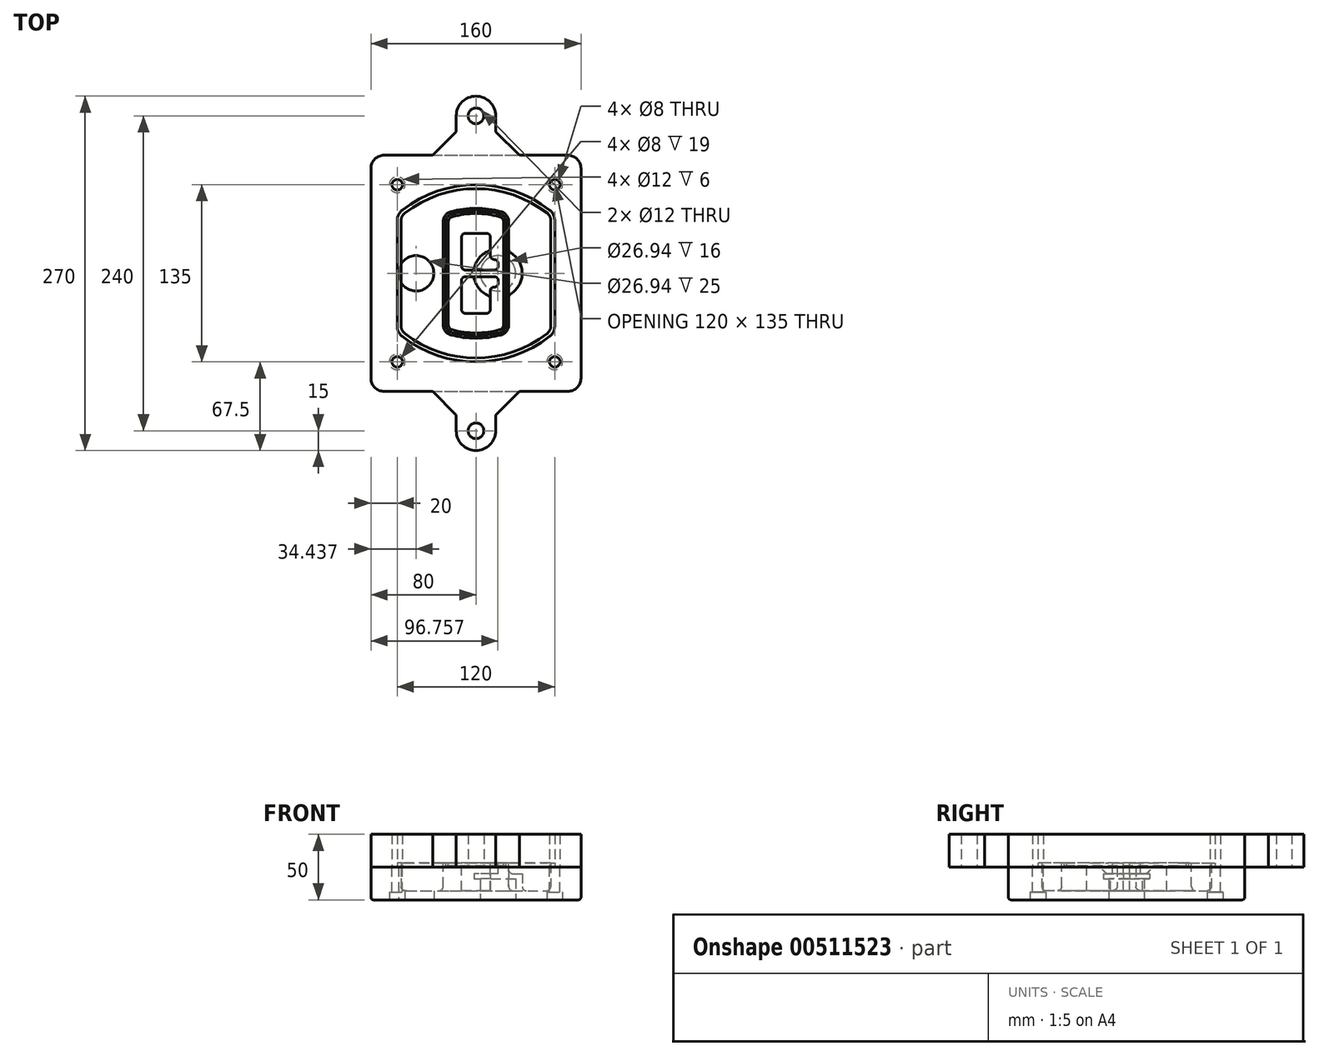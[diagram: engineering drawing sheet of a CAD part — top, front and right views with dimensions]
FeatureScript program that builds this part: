
annotation { "Feature Type Name" : "Feature", "Feature Type Description" : "" }
export const myFeature = defineFeature(function(context is Context, id is Id, definition is map)
    precondition{}
    {
        {
            var Q0;
            Q0=qCreatedBy(makeId("Top.planeOp"),FACE);
            var sketch = newSketch(context, id + "F0", { "sketchPlane" : qUnion([Q0])});
            skPoint(sketch, "E0.rect.middle", {"position": v(0, 0) * mm});
            skLineSegment(sketch, "E1.bottom", {"start": v(-70, -90) * mm, "end": v(70, -90) * mm});
            skLineSegment(sketch, "E1.top", {"start": v(-70, 90) * mm, "end": v(70, 90) * mm});
            skLineSegment(sketch, "E1.left", {"start": v(-80, -80) * mm, "end": v(-80, 80) * mm});
            skLineSegment(sketch, "E1.right", {"start": v(80, -80) * mm, "end": v(80, 80) * mm});
            skLineSegment(sketch, "E2", {"start": v(-80, 90) * mm, "end": v(80, -90) * mm, "construction": true});
            skLineSegment(sketch, "E3", {"start": v(80, 90) * mm, "end": v(-80, -90) * mm, "construction": true});
            skCircle(sketch, "E4", {"center": v(-60, 67.5) * mm, "radius": 4 * mm});
            skCircle(sketch, "E5", {"center": v(60, 67.5) * mm, "radius": 4 * mm});
            skCircle(sketch, "E6", {"center": v(60, -67.5) * mm, "radius": 4 * mm});
            skCircle(sketch, "E7", {"center": v(-60, -67.5) * mm, "radius": 4 * mm});
            skLineSegment(sketch, "E8", {"start": v(-60, 67.5) * mm, "end": v(60, 67.5) * mm, "construction": true});
            skLineSegment(sketch, "E9", {"start": v(60, 67.5) * mm, "end": v(60, -67.5) * mm, "construction": true});
            skLineSegment(sketch, "E10", {"start": v(60, -67.5) * mm, "end": v(-60, -67.5) * mm, "construction": true});
            skLineSegment(sketch, "E11", {"start": v(-60, -67.5) * mm, "end": v(-60, 67.5) * mm, "construction": true});
            skLineSegment(sketch, "E12", {"start": v(-60, 40.3) * mm, "end": v(-60, -40.3) * mm});
            skLineSegment(sketch, "E13", {"start": v(60, 40.3) * mm, "end": v(60, -40.3) * mm});
            skArc(sketch, "E14", {"start": v(56.15, 48.18) * mm, "mid": v(0, 67.5) * mm, "end": v(-56.15, 48.18) * mm});
            skArc(sketch, "E15", {"start": v(-56.15, -48.18) * mm, "mid": v(0, -67.5) * mm, "end": v(56.15, -48.18) * mm});
            skLineSegment(sketch, "E16", {"start": v(-60, 0) * mm, "end": v(60, 0) * mm, "construction": true});
            skPoint(sketch, "E17.visualSharp", {"position": v(-60, -45) * mm});
            skArc(sketch, "E17.filletArc", {"start": v(-60, -40.3) * mm, "mid": v(-58.99, -44.68) * mm, "end": v(-56.15, -48.18) * mm});
            skPoint(sketch, "E18.visualSharp", {"position": v(-60, 45) * mm});
            skArc(sketch, "E18.filletArc", {"start": v(-56.15, 48.18) * mm, "mid": v(-58.99, 44.68) * mm, "end": v(-60, 40.3) * mm});
            skPoint(sketch, "E19.visualSharp", {"position": v(60, 45) * mm});
            skArc(sketch, "E19.filletArc", {"start": v(60, 40.3) * mm, "mid": v(58.99, 44.68) * mm, "end": v(56.15, 48.18) * mm});
            skPoint(sketch, "E20.visualSharp", {"position": v(60, -45) * mm});
            skArc(sketch, "E20.filletArc", {"start": v(56.15, -48.18) * mm, "mid": v(58.99, -44.68) * mm, "end": v(60, -40.3) * mm});
            skPoint(sketch, "E21.visualSharp", {"position": v(-80, 90) * mm});
            skArc(sketch, "E21.filletArc", {"start": v(-70, 90) * mm, "mid": v(-77.07, 87.07) * mm, "end": v(-80, 80) * mm});
            skPoint(sketch, "E22.visualSharp", {"position": v(80, 90) * mm});
            skArc(sketch, "E22.filletArc", {"start": v(80, 80) * mm, "mid": v(77.07, 87.07) * mm, "end": v(70, 90) * mm});
            skPoint(sketch, "E23.visualSharp", {"position": v(80, -90) * mm});
            skArc(sketch, "E23.filletArc", {"start": v(70, -90) * mm, "mid": v(77.07, -87.07) * mm, "end": v(80, -80) * mm});
            skPoint(sketch, "E24.visualSharp", {"position": v(-80, -90) * mm});
            skArc(sketch, "E24.filletArc", {"start": v(-80, -80) * mm, "mid": v(-77.07, -87.07) * mm, "end": v(-70, -90) * mm});
            skArc(sketch, "E25.0", {"start": v(57, 40.3) * mm, "mid": v(56.3, 43.36) * mm, "end": v(54.3, 45.81) * mm});
            skLineSegment(sketch, "E25.1", {"start": v(57, 40.3) * mm, "end": v(57, -40.3) * mm});
            skArc(sketch, "E25.2", {"start": v(54.3, -45.81) * mm, "mid": v(56.3, -43.36) * mm, "end": v(57, -40.3) * mm});
            skArc(sketch, "E25.3", {"start": v(-54.3, -45.81) * mm, "mid": v(0, -64.5) * mm, "end": v(54.3, -45.81) * mm});
            skArc(sketch, "E25.4", {"start": v(-57, -40.3) * mm, "mid": v(-56.3, -43.36) * mm, "end": v(-54.3, -45.81) * mm});
            skArc(sketch, "E25.5", {"start": v(54.3, 45.81) * mm, "mid": v(0, 64.5) * mm, "end": v(-54.3, 45.81) * mm});
            skLineSegment(sketch, "E25.6", {"start": v(-57, 40.3) * mm, "end": v(-57, -40.3) * mm});
            skArc(sketch, "E25.7", {"start": v(-54.3, 45.81) * mm, "mid": v(-56.3, 43.36) * mm, "end": v(-57, 40.3) * mm});
            skArc(sketch, "E26.0", {"start": v(-58.62, 51.33) * mm, "mid": v(-62.58, 46.43) * mm, "end": v(-64, 40.3) * mm});
            skArc(sketch, "E26.1", {"start": v(58.62, 51.33) * mm, "mid": v(0, 71.5) * mm, "end": v(-58.62, 51.33) * mm});
            skArc(sketch, "E26.2", {"start": v(64, 40.3) * mm, "mid": v(62.58, 46.43) * mm, "end": v(58.62, 51.33) * mm});
            skLineSegment(sketch, "E26.3", {"start": v(64, 40.3) * mm, "end": v(64, -40.3) * mm});
            skArc(sketch, "E26.4", {"start": v(58.62, -51.33) * mm, "mid": v(62.58, -46.43) * mm, "end": v(64, -40.3) * mm});
            skLineSegment(sketch, "E26.5", {"start": v(-64, 40.3) * mm, "end": v(-64, -40.3) * mm});
            skArc(sketch, "E26.6", {"start": v(-58.62, -51.33) * mm, "mid": v(0, -71.5) * mm, "end": v(58.62, -51.33) * mm});
            skArc(sketch, "E26.7", {"start": v(-64, -40.3) * mm, "mid": v(-62.58, -46.43) * mm, "end": v(-58.62, -51.33) * mm});
            skSolve(sketch);
        }
        {
            var Q0;
            Q0=makeQuery(id+"F0.imprint","IMPRINT",FACE,{"disambiguationData":[TD([[makeQuery(id+"F0.imprint","IMPRINT",EDGE,{"derivedFrom":sQuery(id+"F0.wireOp",EDGE,"E1.bottom")}),1.0]])]});
            var Q1;
            Q1=makeQuery(id+"F0.imprint","IMPRINT",FACE,{"disambiguationData":[TD([[makeQuery(id+"F0.imprint","IMPRINT",EDGE,{"derivedFrom":sQuery(id+"F0.wireOp",EDGE,"E12")}),1.0]])]});
            var Q2;
            Q2=makeQuery(id+"F0.imprint","IMPRINT",FACE,{"disambiguationData":[TD([[makeQuery(id+"F0.imprint","IMPRINT",EDGE,{"derivedFrom":sQuery(id+"F0.wireOp",EDGE,"E25.0")}),1.0]])]});
            var Q3;
            Q3=makeQuery(id+"F0.imprint","IMPRINT",FACE,{"disambiguationData":[TD([[makeQuery(id+"F0.imprint","IMPRINT",EDGE,{"derivedFrom":sQuery(id+"F0.wireOp",EDGE,"E12")}),-1.0]])]});
            extrude(context, id + "F1", {"entities" : qUnion([Q0, Q1, Q2, Q3]), "oppositeDirection" : true, "depth" : 25 * mm});
        }
        {
            var Q0;
            Q0=makeQuery(id+"F0.imprint","IMPRINT",FACE,{"disambiguationData":[TD([[makeQuery(id+"F0.imprint","IMPRINT",EDGE,{"derivedFrom":sQuery(id+"F0.wireOp",EDGE,"E12")}),1.0]])]});
            extrude(context, id + "F2", {"entities" : qUnion([Q0]), "operationType" : NewBodyOperationType.ADD, "depth" : 3 * mm});
        }
        {
            var Q0;
            Q0=makeQuery(id+"F0.imprint","IMPRINT",FACE,{"disambiguationData":[TD([[makeQuery(id+"F0.imprint","IMPRINT",EDGE,{"derivedFrom":sQuery(id+"F0.wireOp",EDGE,"E25.0")}),1.0]])]});
            extrude(context, id + "F3", {"entities" : qUnion([Q0]), "operationType" : NewBodyOperationType.REMOVE, "oppositeDirection" : true, "depth" : 18 * mm});
        }
        {
            var Q0;
            Q0=makeQuery(id+"F2.opExtrude","CAP_FACE",FACE,{"disambiguationData":[OSD([sQuery(id+"F0.wireOp",EDGE,"E12"),sQuery(id+"F0.wireOp",EDGE,"E13"),sQuery(id+"F0.wireOp",EDGE,"E14"),sQuery(id+"F0.wireOp",EDGE,"E15"),sQuery(id+"F0.wireOp",EDGE,"E17.filletArc"),sQuery(id+"F0.wireOp",EDGE,"E18.filletArc"),sQuery(id+"F0.wireOp",EDGE,"E19.filletArc"),sQuery(id+"F0.wireOp",EDGE,"E20.filletArc"),sQuery(id+"F0.wireOp",EDGE,"E25.0"),sQuery(id+"F0.wireOp",EDGE,"E25.1"),sQuery(id+"F0.wireOp",EDGE,"E25.2"),sQuery(id+"F0.wireOp",EDGE,"E25.3"),sQuery(id+"F0.wireOp",EDGE,"E25.4"),sQuery(id+"F0.wireOp",EDGE,"E25.5"),sQuery(id+"F0.wireOp",EDGE,"E25.6"),sQuery(id+"F0.wireOp",EDGE,"E25.7")])],"isStart":false});
            var sketch = newSketch(context, id + "F4", { "sketchPlane" : qUnion([Q0])});
            skArc(sketch, "E27.0", {"start": v(-19.08, -46.97) * mm, "mid": v(0, -49.5) * mm, "end": v(19.08, -46.97) * mm});
            skArc(sketch, "E28.0", {"start": v(19.08, 46.97) * mm, "mid": v(0, 49.5) * mm, "end": v(-19.08, 46.97) * mm});
            skLineSegment(sketch, "E29", {"start": v(-25, 39.25) * mm, "end": v(-25, -39.25) * mm});
            skLineSegment(sketch, "E30", {"start": v(25, 39.25) * mm, "end": v(25, -39.25) * mm});
            skLineSegment(sketch, "E31", {"start": v(-25, 45.1) * mm, "end": v(25, 45.1) * mm, "construction": true});
            skLineSegment(sketch, "E32", {"start": v(-25, -45.1) * mm, "end": v(25, -45.1) * mm, "construction": true});
            skPoint(sketch, "E33.visualSharp", {"position": v(-25, 45.1) * mm});
            skArc(sketch, "E33.filletArc", {"start": v(-19.08, 46.97) * mm, "mid": v(-23.35, 44.11) * mm, "end": v(-25, 39.25) * mm});
            skPoint(sketch, "E34.visualSharp", {"position": v(25, 45.1) * mm});
            skArc(sketch, "E34.filletArc", {"start": v(25, 39.25) * mm, "mid": v(23.35, 44.11) * mm, "end": v(19.08, 46.97) * mm});
            skPoint(sketch, "E35.visualSharp", {"position": v(25, -45.1) * mm});
            skArc(sketch, "E35.filletArc", {"start": v(19.08, -46.97) * mm, "mid": v(23.35, -44.11) * mm, "end": v(25, -39.25) * mm});
            skPoint(sketch, "E36.visualSharp", {"position": v(-25, -45.1) * mm});
            skArc(sketch, "E36.filletArc", {"start": v(-25, -39.25) * mm, "mid": v(-23.35, -44.11) * mm, "end": v(-19.08, -46.97) * mm});
            skArc(sketch, "E37.0", {"start": v(54.3, 45.81) * mm, "mid": v(0, 64.5) * mm, "end": v(-54.3, 45.81) * mm});
            skArc(sketch, "E37.1", {"start": v(-54.3, 45.81) * mm, "mid": v(-56.3, 43.36) * mm, "end": v(-57, 40.3) * mm});
            skLineSegment(sketch, "E37.2", {"start": v(-57, 40.3) * mm, "end": v(-57, -40.3) * mm});
            skArc(sketch, "E37.3", {"start": v(-57, -40.3) * mm, "mid": v(-56.3, -43.36) * mm, "end": v(-54.3, -45.81) * mm});
            skArc(sketch, "E37.4", {"start": v(-54.3, -45.81) * mm, "mid": v(0, -64.5) * mm, "end": v(54.3, -45.81) * mm});
            skArc(sketch, "E37.5", {"start": v(54.3, -45.81) * mm, "mid": v(56.3, -43.36) * mm, "end": v(57, -40.3) * mm});
            skLineSegment(sketch, "E37.6", {"start": v(57, 40.3) * mm, "end": v(57, -40.3) * mm});
            skArc(sketch, "E37.7", {"start": v(57, 40.3) * mm, "mid": v(56.3, 43.36) * mm, "end": v(54.3, 45.81) * mm});
            skLineSegment(sketch, "E38.0", {"start": v(23, 39.25) * mm, "end": v(23, -39.25) * mm});
            skArc(sketch, "E38.1", {"start": v(18.56, -45.04) * mm, "mid": v(21.76, -42.9) * mm, "end": v(23, -39.25) * mm});
            skArc(sketch, "E38.2", {"start": v(-18.56, -45.04) * mm, "mid": v(0, -47.5) * mm, "end": v(18.56, -45.04) * mm});
            skArc(sketch, "E38.3", {"start": v(-23, -39.25) * mm, "mid": v(-21.76, -42.9) * mm, "end": v(-18.56, -45.04) * mm});
            skLineSegment(sketch, "E38.4", {"start": v(-23, 39.25) * mm, "end": v(-23, -39.25) * mm});
            skArc(sketch, "E38.5", {"start": v(23, 39.25) * mm, "mid": v(21.76, 42.9) * mm, "end": v(18.56, 45.04) * mm});
            skArc(sketch, "E38.6", {"start": v(-18.56, 45.04) * mm, "mid": v(-21.76, 42.9) * mm, "end": v(-23, 39.25) * mm});
            skArc(sketch, "E38.7", {"start": v(18.56, 45.04) * mm, "mid": v(0, 47.5) * mm, "end": v(-18.56, 45.04) * mm});
            skArc(sketch, "E39.0", {"start": v(21, 39.25) * mm, "mid": v(20.18, 41.68) * mm, "end": v(18.04, 43.1) * mm});
            skLineSegment(sketch, "E39.1", {"start": v(21, 39.25) * mm, "end": v(21, -39.25) * mm});
            skArc(sketch, "E39.2", {"start": v(18.04, -43.1) * mm, "mid": v(20.18, -41.68) * mm, "end": v(21, -39.25) * mm});
            skArc(sketch, "E39.3", {"start": v(-18.04, -43.1) * mm, "mid": v(0, -45.5) * mm, "end": v(18.04, -43.1) * mm});
            skArc(sketch, "E39.4", {"start": v(-21, -39.25) * mm, "mid": v(-20.18, -41.68) * mm, "end": v(-18.04, -43.1) * mm});
            skArc(sketch, "E39.5", {"start": v(18.04, 43.1) * mm, "mid": v(0, 45.5) * mm, "end": v(-18.04, 43.1) * mm});
            skLineSegment(sketch, "E39.6", {"start": v(-21, 39.25) * mm, "end": v(-21, -39.25) * mm});
            skArc(sketch, "E39.7", {"start": v(-18.04, 43.1) * mm, "mid": v(-20.18, 41.68) * mm, "end": v(-21, 39.25) * mm});
            skLineSegment(sketch, "E40", {"start": v(-25, 0) * mm, "end": v(25, 0) * mm, "construction": true});
            skLineSegment(sketch, "E41", {"start": v(-11, 5.5) * mm, "end": v(-11, 27.5) * mm});
            skLineSegment(sketch, "E42", {"start": v(-8, 30.5) * mm, "end": v(8, 30.5) * mm});
            skLineSegment(sketch, "E43", {"start": v(11, 27.5) * mm, "end": v(11, 13.5) * mm});
            skLineSegment(sketch, "E44", {"start": v(14, 10.5) * mm, "end": v(14, 10.5) * mm});
            skLineSegment(sketch, "E45", {"start": v(17, 7.5) * mm, "end": v(17, 5.5) * mm});
            skLineSegment(sketch, "E46", {"start": v(14, 2.5) * mm, "end": v(-8, 2.5) * mm});
            skPoint(sketch, "E47.visualSharp", {"position": v(-11, 30.5) * mm});
            skArc(sketch, "E47.filletArc", {"start": v(-8, 30.5) * mm, "mid": v(-10.12, 29.62) * mm, "end": v(-11, 27.5) * mm});
            skPoint(sketch, "E48.visualSharp", {"position": v(11, 30.5) * mm});
            skArc(sketch, "E48.filletArc", {"start": v(11, 27.5) * mm, "mid": v(10.12, 29.62) * mm, "end": v(8, 30.5) * mm});
            skPoint(sketch, "E49.visualSharp", {"position": v(11, 10.5) * mm});
            skArc(sketch, "E49.filletArc", {"start": v(11, 13.5) * mm, "mid": v(11.88, 11.38) * mm, "end": v(14, 10.5) * mm});
            skPoint(sketch, "E50.visualSharp", {"position": v(17, 10.5) * mm});
            skArc(sketch, "E50.filletArc", {"start": v(17, 7.5) * mm, "mid": v(16.12, 9.62) * mm, "end": v(14, 10.5) * mm});
            skPoint(sketch, "E51.visualSharp", {"position": v(17, 2.5) * mm});
            skArc(sketch, "E51.filletArc", {"start": v(14, 2.5) * mm, "mid": v(16.12, 3.38) * mm, "end": v(17, 5.5) * mm});
            skPoint(sketch, "E52.visualSharp", {"position": v(-11, 2.5) * mm});
            skArc(sketch, "E52.filletArc", {"start": v(-11, 5.5) * mm, "mid": v(-10.12, 3.38) * mm, "end": v(-8, 2.5) * mm});
            skLineSegment(sketch, "E53.0.MirrorCS", {"start": v(14, -2.5) * mm, "end": v(-8, -2.5) * mm});
            skArc(sketch, "E54.0.MirrorCS", {"start": v(-11, -5.5) * mm, "mid": v(-10.12, -3.38) * mm, "end": v(-8, -2.5) * mm});
            skLineSegment(sketch, "E55.0.MirrorCS", {"start": v(-11, -5.5) * mm, "end": v(-11, -27.5) * mm});
            skArc(sketch, "E56.0.MirrorCS", {"start": v(-8, -30.5) * mm, "mid": v(-10.12, -29.62) * mm, "end": v(-11, -27.5) * mm});
            skLineSegment(sketch, "E57.0.MirrorCS", {"start": v(-8, -30.5) * mm, "end": v(8, -30.5) * mm});
            skArc(sketch, "E58.0.MirrorCS", {"start": v(11, -27.5) * mm, "mid": v(10.12, -29.62) * mm, "end": v(8, -30.5) * mm});
            skLineSegment(sketch, "E59.0.MirrorCS", {"start": v(11, -27.5) * mm, "end": v(11, -13.5) * mm});
            skArc(sketch, "E60.0.MirrorCS", {"start": v(11, -13.5) * mm, "mid": v(11.88, -11.38) * mm, "end": v(14, -10.5) * mm});
            skArc(sketch, "E61.0.MirrorCS", {"start": v(17, -7.5) * mm, "mid": v(16.12, -9.62) * mm, "end": v(14, -10.5) * mm});
            skLineSegment(sketch, "E62.0.MirrorCS", {"start": v(17, -7.5) * mm, "end": v(17, -5.5) * mm});
            skArc(sketch, "E63.0.MirrorCS", {"start": v(14, -2.5) * mm, "mid": v(16.12, -3.38) * mm, "end": v(17, -5.5) * mm});
            skSolve(sketch);
        }
        {
            var Q0;
            Q0=makeQuery(id+"F4.imprint","IMPRINT",FACE,{"disambiguationData":[TD([[makeQuery(id+"F4.imprint","IMPRINT",EDGE,{"derivedFrom":sQuery(id+"F4.wireOp",EDGE,"E27.0")}),1.0]])]});
            var Q1;
            Q1=makeQuery(id+"F4.imprint","IMPRINT",FACE,{"disambiguationData":[TD([[makeQuery(id+"F4.imprint","IMPRINT",EDGE,{"derivedFrom":sQuery(id+"F4.wireOp",EDGE,"E38.0")}),-1.0]])]});
            var Q2;
            Q2=makeQuery(id+"F4.imprint","IMPRINT",FACE,{"disambiguationData":[TD([[makeQuery(id+"F4.imprint","IMPRINT",EDGE,{"derivedFrom":sQuery(id+"F4.wireOp",EDGE,"E39.0")}),1.0]])]});
            extrude(context, id + "F5", {"entities" : qUnion([Q0, Q1, Q2]), "operationType" : NewBodyOperationType.ADD, "endBound" : BoundingType.UP_TO_NEXT, "oppositeDirection" : true, "depth" : 25 * mm});
        }
        {
            var Q0;
            Q0=makeQuery(id+"F4.imprint","IMPRINT",FACE,{"disambiguationData":[TD([[makeQuery(id+"F4.imprint","IMPRINT",EDGE,{"derivedFrom":sQuery(id+"F4.wireOp",EDGE,"E38.0")}),-1.0]])]});
            extrude(context, id + "F6", {"entities" : qUnion([Q0]), "operationType" : NewBodyOperationType.REMOVE, "oppositeDirection" : true, "depth" : 2 * mm});
        }
        {
            var Q0;
            Q0=makeQuery(id+"F1.opExtrude","CAP_FACE",FACE,{"disambiguationData":[OSD([sQuery(id+"F0.wireOp",EDGE,"E1.bottom"),sQuery(id+"F0.wireOp",EDGE,"E1.top"),sQuery(id+"F0.wireOp",EDGE,"E1.left"),sQuery(id+"F0.wireOp",EDGE,"E1.right"),sQuery(id+"F0.wireOp",EDGE,"E4"),sQuery(id+"F0.wireOp",EDGE,"E5"),sQuery(id+"F0.wireOp",EDGE,"E6"),sQuery(id+"F0.wireOp",EDGE,"E7"),sQuery(id+"F0.wireOp",EDGE,"E21.filletArc"),sQuery(id+"F0.wireOp",EDGE,"E22.filletArc"),sQuery(id+"F0.wireOp",EDGE,"E23.filletArc"),sQuery(id+"F0.wireOp",EDGE,"E24.filletArc")])],"isStart":false});
            var sketch = newSketch(context, id + "F7", { "sketchPlane" : qUnion([Q0])});
            skCircle(sketch, "E64", {"center": v(16.76, 0) * mm, "radius": 13.47 * mm});
            skCircle(sketch, "E65", {"center": v(-45.56, 0) * mm, "radius": 13.47 * mm});
            skLineSegment(sketch, "E66", {"start": v(80, 0) * mm, "end": v(-80, 0) * mm});
            skCircle(sketch, "E67", {"center": v(16.76, 0) * mm, "radius": 18.47 * mm});
            skCircle(sketch, "E68", {"center": v(60, -67.5) * mm, "radius": 6 * mm});
            skCircle(sketch, "E69", {"center": v(-60, -67.5) * mm, "radius": 6 * mm});
            skCircle(sketch, "E70", {"center": v(-60, 67.5) * mm, "radius": 6 * mm});
            skCircle(sketch, "E71", {"center": v(60, 67.5) * mm, "radius": 6 * mm});
            skSolve(sketch);
        }
        {
            var Q0;
            {var subQ1=sQuery(id+"F7.wireOp",EDGE,"E66");var subQ4=sQuery(id+"F7.wireOp",EDGE,"E64");var subQ6=makeQuery(id+"F7.imprint","INTERSECT",VERTEX,{"disambiguationData":[OD(0.0)],"derivedFrom":[subQ4,subQ1]});Q0=makeQuery(id+"F7.imprint","IMPRINT",FACE,{"disambiguationData":[TD([[makeQuery(id+"F7.imprint","IMPRINT",EDGE,{"disambiguationData":[TD([[subQ6,-1.0]])],"derivedFrom":subQ4}),-1.0]])]});}
            var Q1;
            {var subQ0=sQuery(id+"F7.wireOp",EDGE,"E66");var subQ1=sQuery(id+"F7.wireOp",EDGE,"E64");var subQ3=makeQuery(id+"F7.imprint","INTERSECT",VERTEX,{"disambiguationData":[OD(0.0)],"derivedFrom":[subQ1,subQ0]});Q1=makeQuery(id+"F7.imprint","IMPRINT",FACE,{"disambiguationData":[TD([[makeQuery(id+"F7.imprint","IMPRINT",EDGE,{"disambiguationData":[TD([[subQ3,-1.0]])],"derivedFrom":subQ1}),1.0]])]});}
            var Q2;
            {var subQ0=sQuery(id+"F7.wireOp",EDGE,"E66");var subQ1=sQuery(id+"F7.wireOp",EDGE,"E64");var subQ3=makeQuery(id+"F7.imprint","INTERSECT",VERTEX,{"disambiguationData":[OD(0.0)],"derivedFrom":[subQ1,subQ0]});Q2=makeQuery(id+"F7.imprint","IMPRINT",FACE,{"disambiguationData":[TD([[makeQuery(id+"F7.imprint","IMPRINT",EDGE,{"disambiguationData":[TD([[subQ3,1.0]])],"derivedFrom":subQ1}),1.0]])]});}
            var Q3;
            {var subQ1=sQuery(id+"F7.wireOp",EDGE,"E66");var subQ4=sQuery(id+"F7.wireOp",EDGE,"E64");var subQ6=makeQuery(id+"F7.imprint","INTERSECT",VERTEX,{"disambiguationData":[OD(0.0)],"derivedFrom":[subQ4,subQ1]});Q3=makeQuery(id+"F7.imprint","IMPRINT",FACE,{"disambiguationData":[TD([[makeQuery(id+"F7.imprint","IMPRINT",EDGE,{"disambiguationData":[TD([[subQ6,1.0]])],"derivedFrom":subQ4}),-1.0]])]});}
            extrude(context, id + "F8", {"entities" : qUnion([Q0, Q1, Q2, Q3]), "operationType" : NewBodyOperationType.ADD, "oppositeDirection" : true, "depth" : 20 * mm});
        }
        {
            var Q0;
            {var subQ0=sQuery(id+"F7.wireOp",EDGE,"E66");var subQ1=sQuery(id+"F7.wireOp",EDGE,"E64");var subQ3=makeQuery(id+"F7.imprint","INTERSECT",VERTEX,{"disambiguationData":[OD(0.0)],"derivedFrom":[subQ1,subQ0]});Q0=makeQuery(id+"F7.imprint","IMPRINT",FACE,{"disambiguationData":[TD([[makeQuery(id+"F7.imprint","IMPRINT",EDGE,{"disambiguationData":[TD([[subQ3,-1.0]])],"derivedFrom":subQ1}),1.0]])]});}
            var Q1;
            {var subQ0=sQuery(id+"F7.wireOp",EDGE,"E66");var subQ1=sQuery(id+"F7.wireOp",EDGE,"E64");var subQ3=makeQuery(id+"F7.imprint","INTERSECT",VERTEX,{"disambiguationData":[OD(0.0)],"derivedFrom":[subQ1,subQ0]});Q1=makeQuery(id+"F7.imprint","IMPRINT",FACE,{"disambiguationData":[TD([[makeQuery(id+"F7.imprint","IMPRINT",EDGE,{"disambiguationData":[TD([[subQ3,1.0]])],"derivedFrom":subQ1}),1.0]])]});}
            extrude(context, id + "F9", {"entities" : qUnion([Q0, Q1]), "operationType" : NewBodyOperationType.REMOVE, "oppositeDirection" : true, "depth" : 16 * mm});
        }
        {
            var Q0;
            {var subQ0=sQuery(id+"F7.wireOp",EDGE,"E66");var subQ1=sQuery(id+"F7.wireOp",EDGE,"E65");var subQ3=makeQuery(id+"F7.imprint","INTERSECT",VERTEX,{"disambiguationData":[OD(0.0)],"derivedFrom":[subQ1,subQ0]});Q0=makeQuery(id+"F7.imprint","IMPRINT",FACE,{"disambiguationData":[TD([[makeQuery(id+"F7.imprint","IMPRINT",EDGE,{"disambiguationData":[TD([[subQ3,-1.0]])],"derivedFrom":subQ1}),1.0]])]});}
            var Q1;
            {var subQ0=sQuery(id+"F7.wireOp",EDGE,"E66");var subQ1=sQuery(id+"F7.wireOp",EDGE,"E65");var subQ3=makeQuery(id+"F7.imprint","INTERSECT",VERTEX,{"disambiguationData":[OD(0.0)],"derivedFrom":[subQ1,subQ0]});Q1=makeQuery(id+"F7.imprint","IMPRINT",FACE,{"disambiguationData":[TD([[makeQuery(id+"F7.imprint","IMPRINT",EDGE,{"disambiguationData":[TD([[subQ3,1.0]])],"derivedFrom":subQ1}),1.0]])]});}
            extrude(context, id + "F10", {"entities" : qUnion([Q0, Q1]), "operationType" : NewBodyOperationType.REMOVE, "oppositeDirection" : true, "depth" : 25 * mm});
        }
        {
            var Q0;
            Q0=makeQuery(id+"F7.imprint","IMPRINT",FACE,{"disambiguationData":[TD([[makeQuery(id+"F7.imprint","IMPRINT",EDGE,{"derivedFrom":sQuery(id+"F7.wireOp",EDGE,"E68")}),1.0]])]});
            var Q1;
            Q1=makeQuery(id+"F7.imprint","IMPRINT",FACE,{"disambiguationData":[TD([[makeQuery(id+"F7.imprint","IMPRINT",EDGE,{"derivedFrom":makeQuery(id+"F1.opExtrude","CAP_EDGE",EDGE,{"disambiguationData":[OSD([sQuery(id+"F0.wireOp",EDGE,"E5")])],"isStart":false})}),-1.0]])]});
            var Q2;
            Q2=makeQuery(id+"F7.imprint","IMPRINT",FACE,{"disambiguationData":[TD([[makeQuery(id+"F7.imprint","IMPRINT",EDGE,{"derivedFrom":sQuery(id+"F7.wireOp",EDGE,"E69")}),1.0]])]});
            var Q3;
            Q3=makeQuery(id+"F7.imprint","IMPRINT",FACE,{"disambiguationData":[TD([[makeQuery(id+"F7.imprint","IMPRINT",EDGE,{"derivedFrom":makeQuery(id+"F1.opExtrude","CAP_EDGE",EDGE,{"disambiguationData":[OSD([sQuery(id+"F0.wireOp",EDGE,"E4")])],"isStart":false})}),-1.0]])]});
            var Q4;
            Q4=makeQuery(id+"F7.imprint","IMPRINT",FACE,{"disambiguationData":[TD([[makeQuery(id+"F7.imprint","IMPRINT",EDGE,{"derivedFrom":sQuery(id+"F7.wireOp",EDGE,"E70")}),1.0]])]});
            var Q5;
            Q5=makeQuery(id+"F7.imprint","IMPRINT",FACE,{"disambiguationData":[TD([[makeQuery(id+"F7.imprint","IMPRINT",EDGE,{"derivedFrom":makeQuery(id+"F1.opExtrude","CAP_EDGE",EDGE,{"disambiguationData":[OSD([sQuery(id+"F0.wireOp",EDGE,"E7")])],"isStart":false})}),-1.0]])]});
            var Q6;
            Q6=makeQuery(id+"F7.imprint","IMPRINT",FACE,{"disambiguationData":[TD([[makeQuery(id+"F7.imprint","IMPRINT",EDGE,{"derivedFrom":sQuery(id+"F7.wireOp",EDGE,"E71")}),1.0]])]});
            var Q7;
            Q7=makeQuery(id+"F7.imprint","IMPRINT",FACE,{"disambiguationData":[TD([[makeQuery(id+"F7.imprint","IMPRINT",EDGE,{"derivedFrom":makeQuery(id+"F1.opExtrude","CAP_EDGE",EDGE,{"disambiguationData":[OSD([sQuery(id+"F0.wireOp",EDGE,"E6")])],"isStart":false})}),-1.0]])]});
            extrude(context, id + "F11", {"entities" : qUnion([Q0, Q1, Q2, Q3, Q4, Q5, Q6, Q7]), "operationType" : NewBodyOperationType.REMOVE, "oppositeDirection" : true, "depth" : 6 * mm});
        }
        {
            var Q0;
            Q0=makeQuery(id+"F9.boolean.opBoolean","COPY",FACE,{"derivedFrom":makeQuery(id+"F9.opExtrude","CAP_FACE",FACE,{"disambiguationData":[OSD([sQuery(id+"F7.wireOp",EDGE,"E64")])],"isStart":false})});
            var sketch = newSketch(context, id + "F12", { "sketchPlane" : qUnion([Q0])});
            skArc(sketch, "E72.0", {"start": v(11, 17.55) * mm, "mid": v(2.57, 11.82) * mm, "end": v(-1.54, 2.5) * mm});
            skArc(sketch, "E72.1", {"start": v(-1.54, -2.5) * mm, "mid": v(2.57, -11.82) * mm, "end": v(11, -17.55) * mm});
            skLineSegment(sketch, "E73", {"start": v(-1.54, -2.5) * mm, "end": v(14, -2.5) * mm});
            skLineSegment(sketch, "E74.0", {"start": v(14, 2.5) * mm, "end": v(-1.54, 2.5) * mm});
            skArc(sketch, "E74.1", {"start": v(14, 2.5) * mm, "mid": v(16.12, 3.38) * mm, "end": v(17, 5.5) * mm});
            skLineSegment(sketch, "E74.2", {"start": v(17, 7.5) * mm, "end": v(17, 5.5) * mm});
            skArc(sketch, "E74.3", {"start": v(17, 7.5) * mm, "mid": v(16.12, 9.62) * mm, "end": v(14, 10.5) * mm});
            skArc(sketch, "E74.4", {"start": v(11, 13.5) * mm, "mid": v(11.88, 11.38) * mm, "end": v(14, 10.5) * mm});
            skLineSegment(sketch, "E74.5", {"start": v(11, 17.55) * mm, "end": v(11, 13.5) * mm});
            skLineSegment(sketch, "E74.7", {"start": v(14, -2.5) * mm, "end": v(-1.54, -2.5) * mm});
            skArc(sketch, "E74.8", {"start": v(14, -2.5) * mm, "mid": v(16.12, -3.38) * mm, "end": v(17, -5.5) * mm});
            skLineSegment(sketch, "E74.9", {"start": v(17, -7.5) * mm, "end": v(17, -5.5) * mm});
            skArc(sketch, "E74.10", {"start": v(17, -7.5) * mm, "mid": v(16.12, -9.62) * mm, "end": v(14, -10.5) * mm});
            skArc(sketch, "E74.11", {"start": v(11, -13.5) * mm, "mid": v(11.88, -11.38) * mm, "end": v(14, -10.5) * mm});
            skLineSegment(sketch, "E74.12", {"start": v(11, -17.55) * mm, "end": v(11, -13.5) * mm});
            skPoint(sketch, "E75.orphan", {"position": v(11, -27.5) * mm});
            skPoint(sketch, "E76.orphan", {"position": v(-8, -2.5) * mm});
            skPoint(sketch, "E77.orphan", {"position": v(-8, 2.5) * mm});
            skPoint(sketch, "E78.orphan", {"position": v(11, 27.5) * mm});
            skSolve(sketch);
        }
        {
            var Q0;
            {var subQ7=sQuery(id+"F12.wireOp",EDGE,"E72.0");var subQ14=sQuery(id+"F12.wireOp",EDGE,"E72.1");var subQ16=sQuery(id+"F12.wireOp",EDGE,"E74.1");var subQ18=sQuery(id+"F12.wireOp",EDGE,"E74.8");Q0=qUnion([makeQuery(id+"F12.imprint","IMPRINT",FACE,{"disambiguationData":[TD([[makeQuery(id+"F12.imprint","IMPRINT",EDGE,{"derivedFrom":subQ7}),1.0]])]}),makeQuery(id+"F12.imprint","IMPRINT",FACE,{"disambiguationData":[TD([[makeQuery(id+"F12.imprint","IMPRINT",EDGE,{"derivedFrom":subQ14}),1.0]])]}),makeQuery(id+"F12.imprint","IMPRINT",FACE,{"disambiguationData":[TD([[makeQuery(id+"F12.imprint","IMPRINT",EDGE,{"derivedFrom":subQ16}),1.0]])]}),makeQuery(id+"F12.imprint","IMPRINT",FACE,{"disambiguationData":[TD([[makeQuery(id+"F12.imprint","IMPRINT",EDGE,{"derivedFrom":subQ18}),-1.0]])]})]);}
            var Q1;
            Q1=makeQuery(id+"F5.boolean.opBoolean","SPLIT",FACE,{"disambiguationData":[TD([makeQuery(id+"F5.opExtrude","SWEPT_FACE",FACE,{"disambiguationData":[OSD([sQuery(id+"F4.wireOp",EDGE,"E41")])]})])],"derivedFrom":makeQuery(id+"F3.boolean.opBoolean","COPY",FACE,{"derivedFrom":makeQuery(id+"F3.opExtrude","CAP_FACE",FACE,{"disambiguationData":[OSD([sQuery(id+"F0.wireOp",EDGE,"E25.0"),sQuery(id+"F0.wireOp",EDGE,"E25.1"),sQuery(id+"F0.wireOp",EDGE,"E25.2"),sQuery(id+"F0.wireOp",EDGE,"E25.3"),sQuery(id+"F0.wireOp",EDGE,"E25.4"),sQuery(id+"F0.wireOp",EDGE,"E25.5"),sQuery(id+"F0.wireOp",EDGE,"E25.6"),sQuery(id+"F0.wireOp",EDGE,"E25.7")])],"isStart":false})})});
            extrude(context, id + "F13", {"entities" : qUnion([Q0]), "operationType" : NewBodyOperationType.REMOVE, "endBound" : BoundingType.UP_TO_SURFACE, "endBoundEntityFace" : qUnion([Q1]), "depth" : 25 * mm});
        }
        {
            var Q0;
            Q0=makeQuery(id+"F3.boolean.opBoolean","COPY",EDGE,{"derivedFrom":makeQuery(id+"F3.opExtrude","CAP_EDGE",EDGE,{"disambiguationData":[OSD([sQuery(id+"F0.wireOp",EDGE,"E25.6")])],"isStart":false})});
            var Q1;
            Q1=makeQuery(id+"F8.boolean.opBoolean","INTERSECT",EDGE,{"derivedFrom":[makeQuery(id+"F5.opExtrude","SWEPT_FACE",FACE,{"disambiguationData":[OSD([sQuery(id+"F4.wireOp",EDGE,"E30")])]}),makeQuery(id+"F8.opExtrude","CAP_FACE",FACE,{"disambiguationData":[OSD([sQuery(id+"F7.wireOp",EDGE,"E67")])],"isStart":false})]});
            var Q2;
            Q2=makeQuery(id+"F8.boolean.opBoolean","INTERSECT",EDGE,{"disambiguationData":[OD(1.0)],"derivedFrom":[makeQuery(id+"F5.opExtrude","SWEPT_FACE",FACE,{"disambiguationData":[OSD([sQuery(id+"F4.wireOp",EDGE,"E30")])]}),makeQuery(id+"F8.opExtrude","SWEPT_FACE",FACE,{"disambiguationData":[OSD([sQuery(id+"F7.wireOp",EDGE,"E67")])]})]});
            var Q3;
            {var subQ0=sQuery(id+"F4.wireOp",EDGE,"E30");Q3=makeQuery(id+"F8.boolean.opBoolean","SPLIT",EDGE,{"disambiguationData":[TD([makeQuery(id+"F5.opExtrude","SWEPT_FACE",FACE,{"disambiguationData":[OSD([sQuery(id+"F4.wireOp",EDGE,"E35.filletArc")])]})])],"derivedFrom":makeQuery(id+"F5.opExtrude","CAP_EDGE",EDGE,{"disambiguationData":[OSD([subQ0])],"isStart":false})});}
            var Q4;
            {var subQ0=sQuery(id+"F0.wireOp",EDGE,"E25.7");var subQ1=sQuery(id+"F0.wireOp",EDGE,"E25.1");var subQ2=sQuery(id+"F0.wireOp",EDGE,"E25.6");var subQ3=sQuery(id+"F0.wireOp",EDGE,"E25.5");var subQ4=sQuery(id+"F0.wireOp",EDGE,"E25.4");var subQ5=sQuery(id+"F0.wireOp",EDGE,"E25.0");var subQ6=sQuery(id+"F0.wireOp",EDGE,"E25.2");var subQ7=sQuery(id+"F0.wireOp",EDGE,"E25.3");Q4=makeQuery(id+"F8.boolean.opBoolean","INTERSECT",EDGE,{"derivedFrom":[makeQuery(id+"F5.boolean.opBoolean","SPLIT",FACE,{"disambiguationData":[TD([makeQuery(id+"F2.opExtrude","SWEPT_FACE",FACE,{"disambiguationData":[OSD([subQ5])]})])],"derivedFrom":makeQuery(id+"F3.boolean.opBoolean","COPY",FACE,{"derivedFrom":makeQuery(id+"F3.opExtrude","CAP_FACE",FACE,{"disambiguationData":[OSD([subQ5,subQ1,subQ6,subQ7,subQ4,subQ3,subQ2,subQ0])],"isStart":false})})}),makeQuery(id+"F8.opExtrude","SWEPT_FACE",FACE,{"disambiguationData":[OSD([sQuery(id+"F7.wireOp",EDGE,"E67")])]})]});}
            var Q5;
            Q5=makeQuery(id+"F8.boolean.opBoolean","INTERSECT",EDGE,{"disambiguationData":[OD(0.0)],"derivedFrom":[makeQuery(id+"F5.opExtrude","SWEPT_FACE",FACE,{"disambiguationData":[OSD([sQuery(id+"F4.wireOp",EDGE,"E30")])]}),makeQuery(id+"F8.opExtrude","SWEPT_FACE",FACE,{"disambiguationData":[OSD([sQuery(id+"F7.wireOp",EDGE,"E67")])]})]});
            fillet(context, id + "F14", {"entities" : qUnion([Q0, Q1, Q2, Q3, Q4, Q5]), "radius" : 3 * mm, "tangentPropagation" : true, "allowEdgeOverflow" : false});
        }
        {
            var Q0;
            Q0=makeQuery(id+"F1.opExtrude","CAP_EDGE",EDGE,{"disambiguationData":[OSD([sQuery(id+"F0.wireOp",EDGE,"E1.bottom")])],"isStart":false});
            fillet(context, id + "F15", {"entities" : qUnion([Q0]), "radius" : 2 * mm, "tangentPropagation" : true, "allowEdgeOverflow" : false});
        }
        {
            var Q0;
            {var subQ0=sQuery(id+"F0.wireOp",EDGE,"E21.filletArc");var subQ1=sQuery(id+"F0.wireOp",EDGE,"E7");var subQ2=sQuery(id+"F0.wireOp",EDGE,"E6");var subQ3=sQuery(id+"F0.wireOp",EDGE,"E5");var subQ4=sQuery(id+"F0.wireOp",EDGE,"E4");var subQ5=sQuery(id+"F0.wireOp",EDGE,"E22.filletArc");var subQ6=sQuery(id+"F0.wireOp",EDGE,"E1.bottom");var subQ7=sQuery(id+"F0.wireOp",EDGE,"E1.right");var subQ8=sQuery(id+"F0.wireOp",EDGE,"E1.top");var subQ9=sQuery(id+"F0.wireOp",EDGE,"E1.left");var subQ10=sQuery(id+"F0.wireOp",EDGE,"E23.filletArc");var subQ11=sQuery(id+"F0.wireOp",EDGE,"E24.filletArc");Q0=makeQuery(id+"F2.boolean.opBoolean","SPLIT",FACE,{"disambiguationData":[TD([makeQuery(id+"F1.opExtrude","SWEPT_FACE",FACE,{"disambiguationData":[OSD([subQ6])]})])],"derivedFrom":makeQuery(id+"F1.opExtrude","CAP_FACE",FACE,{"disambiguationData":[OSD([subQ6,subQ8,subQ9,subQ7,subQ4,subQ3,subQ2,subQ1,subQ0,subQ5,subQ10,subQ11])],"isStart":true})});}
            var sketch = newSketch(context, id + "F16", { "sketchPlane" : qUnion([Q0])});
            skLineSegment(sketch, "E79.0", {"start": v(-70, 90) * mm, "end": v(70, 90) * mm});
            skArc(sketch, "E79.1", {"start": v(-70, 90) * mm, "mid": v(-77.07, 87.07) * mm, "end": v(-80, 80) * mm});
            skLineSegment(sketch, "E79.2", {"start": v(-80, -80) * mm, "end": v(-80, 80) * mm});
            skArc(sketch, "E79.3", {"start": v(-80, -80) * mm, "mid": v(-77.07, -87.07) * mm, "end": v(-70, -90) * mm});
            skLineSegment(sketch, "E79.4", {"start": v(-70, -90) * mm, "end": v(70, -90) * mm});
            skArc(sketch, "E79.5", {"start": v(70, -90) * mm, "mid": v(77.07, -87.07) * mm, "end": v(80, -80) * mm});
            skLineSegment(sketch, "E79.6", {"start": v(80, -80) * mm, "end": v(80, 80) * mm});
            skArc(sketch, "E79.7", {"start": v(80, 80) * mm, "mid": v(77.07, 87.07) * mm, "end": v(70, 90) * mm});
            skCircle(sketch, "E79.8", {"center": v(60, 67.5) * mm, "radius": 4 * mm});
            skCircle(sketch, "E79.9", {"center": v(-60, 67.5) * mm, "radius": 4 * mm});
            skCircle(sketch, "E79.10", {"center": v(-60, -67.5) * mm, "radius": 4 * mm});
            skCircle(sketch, "E79.11", {"center": v(60, -67.5) * mm, "radius": 4 * mm});
            skArc(sketch, "E79.12", {"start": v(-56.15, -48.18) * mm, "mid": v(0, -67.5) * mm, "end": v(56.15, -48.18) * mm});
            skLineSegment(sketch, "E79.13", {"start": v(60, 40.3) * mm, "end": v(60, -40.3) * mm});
            skArc(sketch, "E79.14", {"start": v(56.15, 48.18) * mm, "mid": v(0, 67.5) * mm, "end": v(-56.15, 48.18) * mm});
            skLineSegment(sketch, "E79.15", {"start": v(-60, 40.3) * mm, "end": v(-60, -40.3) * mm});
            skArc(sketch, "E79.16", {"start": v(-56.15, 48.18) * mm, "mid": v(-58.99, 44.68) * mm, "end": v(-60, 40.3) * mm});
            skArc(sketch, "E79.17", {"start": v(60, 40.3) * mm, "mid": v(58.99, 44.68) * mm, "end": v(56.15, 48.18) * mm});
            skArc(sketch, "E79.18", {"start": v(56.15, -48.18) * mm, "mid": v(58.99, -44.68) * mm, "end": v(60, -40.3) * mm});
            skArc(sketch, "E79.19", {"start": v(-60, -40.3) * mm, "mid": v(-58.99, -44.68) * mm, "end": v(-56.15, -48.18) * mm});
            skLineSegment(sketch, "E80", {"start": v(-33, 90) * mm, "end": v(-15, 108) * mm});
            skLineSegment(sketch, "E81", {"start": v(-15, 108) * mm, "end": v(-15, 120) * mm});
            skLineSegment(sketch, "E82", {"start": v(33, 90) * mm, "end": v(15, 108) * mm});
            skLineSegment(sketch, "E83", {"start": v(15, 108) * mm, "end": v(15, 120) * mm});
            skArc(sketch, "E84", {"start": v(15, 120) * mm, "mid": v(0, 135) * mm, "end": v(-15, 120) * mm});
            skCircle(sketch, "E85", {"center": v(0, 120) * mm, "radius": 6 * mm});
            skLineSegment(sketch, "E86", {"start": v(0, 90) * mm, "end": v(0, 120) * mm, "construction": true});
            skLineSegment(sketch, "E87", {"start": v(-80, 0) * mm, "end": v(80, 0) * mm, "construction": true});
            skLineSegment(sketch, "E88.MirrorCS", {"start": v(0, -90) * mm, "end": v(0, -120) * mm, "construction": true});
            skLineSegment(sketch, "E89.MirrorCS", {"start": v(-33, -90) * mm, "end": v(-15, -108) * mm});
            skLineSegment(sketch, "E90.MirrorCS", {"start": v(-15, -108) * mm, "end": v(-15, -120) * mm});
            skCircle(sketch, "E91.MirrorC", {"center": v(0, -120) * mm, "radius": 6 * mm});
            skArc(sketch, "E92.MirrorCS", {"start": v(15, -120) * mm, "mid": v(0, -135) * mm, "end": v(-15, -120) * mm});
            skLineSegment(sketch, "E93.MirrorCS", {"start": v(15, -108) * mm, "end": v(15, -120) * mm});
            skLineSegment(sketch, "E94.MirrorCS", {"start": v(33, -90) * mm, "end": v(15, -108) * mm});
            skSolve(sketch);
        }
        {
            var Q0;
            Q0 = qSketchRegion(id + "F16", true);
            extrude(context, id + "F17", {"entities" : qUnion([Q0]), "depth" : 25 * mm});
        }
    });
